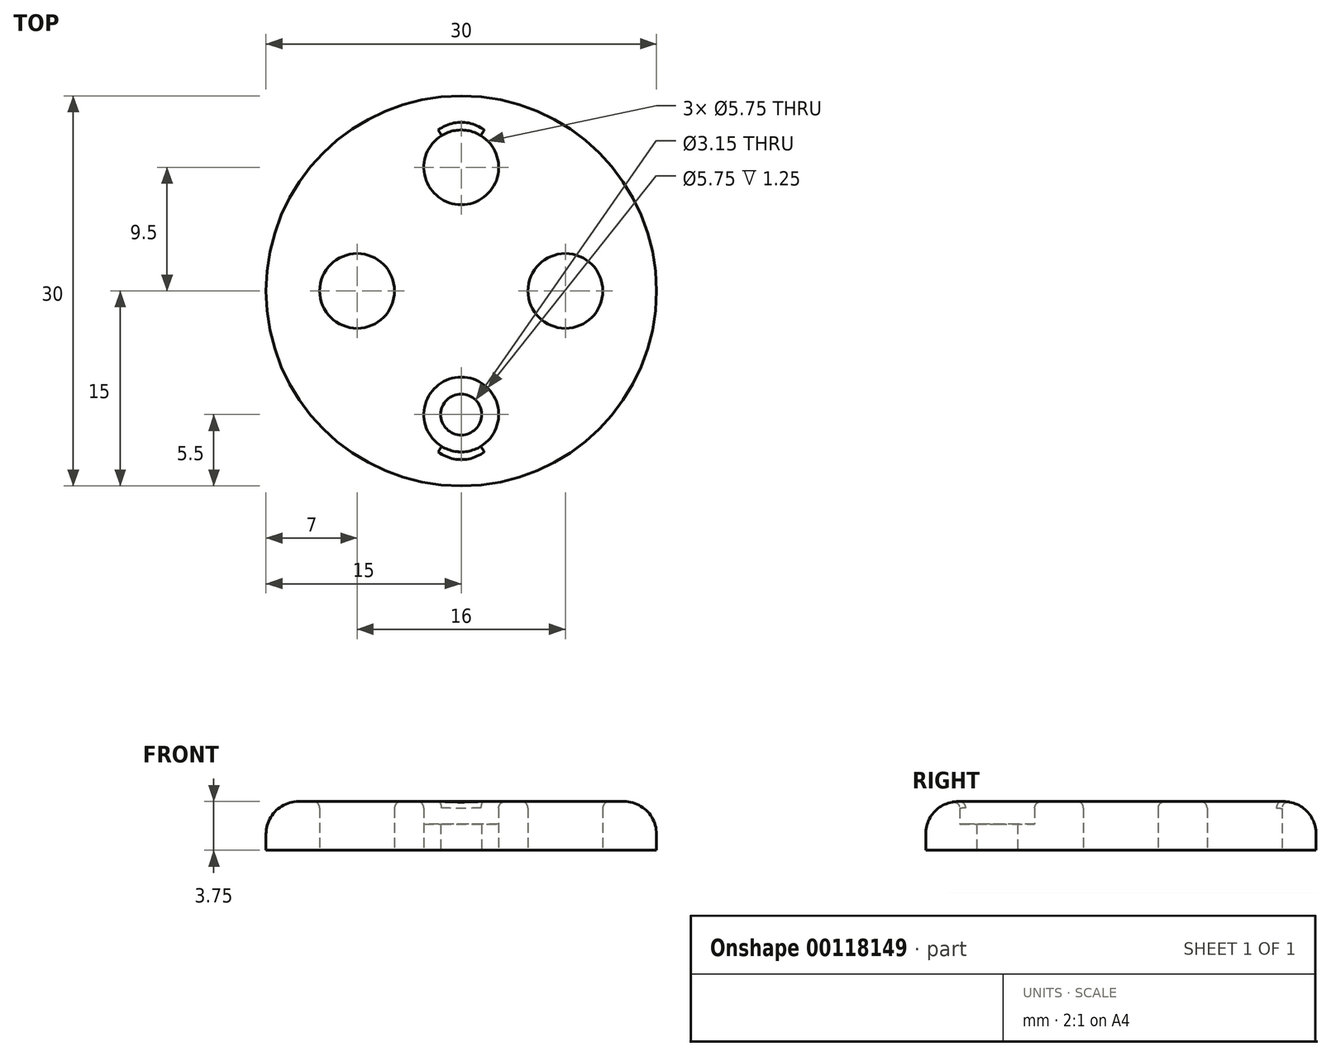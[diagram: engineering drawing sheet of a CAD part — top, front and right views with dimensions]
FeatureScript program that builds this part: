
annotation { "Feature Type Name" : "Feature", "Feature Type Description" : "" }
export const myFeature = defineFeature(function(context is Context, id is Id, definition is map)
    precondition{}
    {
        {
            var Q0;
            Q0=qCreatedBy(makeId("Top.planeOp"),FACE);
            var sketch = newSketch(context, id + "F0", { "sketchPlane" : qUnion([Q0])});
            skCircle(sketch, "E0", {"center": v(0, 0) * mm, "radius": 15 * mm});
            skLineSegment(sketch, "E1", {"start": v(0, 15) * mm, "end": v(0, -15) * mm});
            skLineSegment(sketch, "E2", {"start": v(-19.9, 0) * mm, "end": v(23, 0) * mm});
            skCircle(sketch, "E3", {"center": v(-8, 0) * mm, "radius": 1.57 * mm});
            skCircle(sketch, "E4", {"center": v(0, 9.5) * mm, "radius": 1.57 * mm});
            skCircle(sketch, "E5", {"center": v(8, 0) * mm, "radius": 1.57 * mm});
            skCircle(sketch, "E6", {"center": v(0, -9.5) * mm, "radius": 1.57 * mm});
            skCircle(sketch, "E7", {"center": v(-8, 0) * mm, "radius": 2.88 * mm});
            skCircle(sketch, "E8", {"center": v(0, -9.5) * mm, "radius": 2.88 * mm});
            skCircle(sketch, "E9", {"center": v(8, 0) * mm, "radius": 2.88 * mm});
            skCircle(sketch, "E10", {"center": v(0, 9.5) * mm, "radius": 2.88 * mm});
            skSolve(sketch);
        }
        {
            var Q0;
            Q0=qSketchRegion(id+"F0",true);
            var Q1;
            {var subQ1=sQuery(id+"F0.wireOp",EDGE,"E0");var subQ6=sQuery(id+"F0.wireOp",EDGE,"E1");var subQ9=makeQuery(id+"F0.imprint","INTERSECT",VERTEX,{"disambiguationData":[OD(0.0)],"derivedFrom":[subQ1,subQ6]});Q1=makeQuery(id+"F0.imprint","IMPRINT",FACE,{"disambiguationData":[TD([[makeQuery(id+"F0.imprint","IMPRINT",EDGE,{"disambiguationData":[TD([[subQ9,-1.0]])],"derivedFrom":subQ1}),1.0]])]});}
            var Q2;
            {var subQ0=sQuery(id+"F0.wireOp",EDGE,"E2");var subQ1=sQuery(id+"F0.wireOp",EDGE,"E0");var subQ2=makeQuery(id+"F0.imprint","INTERSECT",VERTEX,{"disambiguationData":[OD(1.0)],"derivedFrom":[subQ1,subQ0]});Q2=makeQuery(id+"F0.imprint","IMPRINT",FACE,{"disambiguationData":[TD([[makeQuery(id+"F0.imprint","IMPRINT",EDGE,{"disambiguationData":[TD([[subQ2,-1.0]])],"derivedFrom":subQ1}),1.0]])]});}
            var Q3;
            {var subQ0=sQuery(id+"F0.wireOp",EDGE,"E7");var subQ1=sQuery(id+"F0.wireOp",EDGE,"E2");var subQ2=makeQuery(id+"F0.imprint","INTERSECT",VERTEX,{"disambiguationData":[OD(0.0)],"derivedFrom":[subQ1,subQ0]});Q3=makeQuery(id+"F0.imprint","IMPRINT",FACE,{"disambiguationData":[TD([[makeQuery(id+"F0.imprint","IMPRINT",EDGE,{"disambiguationData":[TD([[subQ2,-1.0]])],"derivedFrom":subQ1}),1.0]])]});}
            var Q4;
            {var subQ0=sQuery(id+"F0.wireOp",EDGE,"E7");var subQ1=sQuery(id+"F0.wireOp",EDGE,"E2");var subQ2=makeQuery(id+"F0.imprint","INTERSECT",VERTEX,{"disambiguationData":[OD(0.0)],"derivedFrom":[subQ1,subQ0]});Q4=makeQuery(id+"F0.imprint","IMPRINT",FACE,{"disambiguationData":[TD([[makeQuery(id+"F0.imprint","IMPRINT",EDGE,{"disambiguationData":[TD([[subQ2,-1.0]])],"derivedFrom":subQ1}),-1.0]])]});}
            var Q5;
            {var subQ0=sQuery(id+"F0.wireOp",EDGE,"E8");var subQ1=sQuery(id+"F0.wireOp",EDGE,"E1");var subQ2=makeQuery(id+"F0.imprint","INTERSECT",VERTEX,{"disambiguationData":[OD(0.0)],"derivedFrom":[subQ1,subQ0]});Q5=makeQuery(id+"F0.imprint","IMPRINT",FACE,{"disambiguationData":[TD([[makeQuery(id+"F0.imprint","IMPRINT",EDGE,{"disambiguationData":[TD([[subQ2,-1.0]])],"derivedFrom":subQ1}),-1.0]])]});}
            var Q6;
            {var subQ0=sQuery(id+"F0.wireOp",EDGE,"E8");var subQ1=sQuery(id+"F0.wireOp",EDGE,"E1");var subQ2=makeQuery(id+"F0.imprint","INTERSECT",VERTEX,{"disambiguationData":[OD(0.0)],"derivedFrom":[subQ1,subQ0]});Q6=makeQuery(id+"F0.imprint","IMPRINT",FACE,{"disambiguationData":[TD([[makeQuery(id+"F0.imprint","IMPRINT",EDGE,{"disambiguationData":[TD([[subQ2,-1.0]])],"derivedFrom":subQ1}),1.0]])]});}
            var Q7;
            {var subQ0=sQuery(id+"F0.wireOp",EDGE,"E9");var subQ1=sQuery(id+"F0.wireOp",EDGE,"E2");var subQ2=makeQuery(id+"F0.imprint","INTERSECT",VERTEX,{"disambiguationData":[OD(0.0)],"derivedFrom":[subQ1,subQ0]});Q7=makeQuery(id+"F0.imprint","IMPRINT",FACE,{"disambiguationData":[TD([[makeQuery(id+"F0.imprint","IMPRINT",EDGE,{"disambiguationData":[TD([[subQ2,-1.0]])],"derivedFrom":subQ1}),-1.0]])]});}
            var Q8;
            {var subQ0=sQuery(id+"F0.wireOp",EDGE,"E9");var subQ1=sQuery(id+"F0.wireOp",EDGE,"E2");var subQ2=makeQuery(id+"F0.imprint","INTERSECT",VERTEX,{"disambiguationData":[OD(0.0)],"derivedFrom":[subQ1,subQ0]});Q8=makeQuery(id+"F0.imprint","IMPRINT",FACE,{"disambiguationData":[TD([[makeQuery(id+"F0.imprint","IMPRINT",EDGE,{"disambiguationData":[TD([[subQ2,-1.0]])],"derivedFrom":subQ1}),1.0]])]});}
            var Q9;
            {var subQ0=sQuery(id+"F0.wireOp",EDGE,"E10");var subQ1=sQuery(id+"F0.wireOp",EDGE,"E1");var subQ2=makeQuery(id+"F0.imprint","INTERSECT",VERTEX,{"disambiguationData":[OD(0.0)],"derivedFrom":[subQ1,subQ0]});Q9=makeQuery(id+"F0.imprint","IMPRINT",FACE,{"disambiguationData":[TD([[makeQuery(id+"F0.imprint","IMPRINT",EDGE,{"disambiguationData":[TD([[subQ2,-1.0]])],"derivedFrom":subQ1}),1.0]])]});}
            var Q10;
            {var subQ0=sQuery(id+"F0.wireOp",EDGE,"E10");var subQ1=sQuery(id+"F0.wireOp",EDGE,"E1");var subQ2=makeQuery(id+"F0.imprint","INTERSECT",VERTEX,{"disambiguationData":[OD(0.0)],"derivedFrom":[subQ1,subQ0]});Q10=makeQuery(id+"F0.imprint","IMPRINT",FACE,{"disambiguationData":[TD([[makeQuery(id+"F0.imprint","IMPRINT",EDGE,{"disambiguationData":[TD([[subQ2,-1.0]])],"derivedFrom":subQ1}),-1.0]])]});}
            extrude(context, id + "F1", {"entities" : qUnion([Q0, Q1, Q2, Q3, Q4, Q5, Q6, Q7, Q8, Q9, Q10]), "depth" : 2 * mm});
        }
        {
            var Q0;
            {var subQ1=sQuery(id+"F0.wireOp",EDGE,"E0");var subQ5=sQuery(id+"F0.wireOp",EDGE,"E1");var subQ10=makeQuery(id+"F0.imprint","INTERSECT",VERTEX,{"disambiguationData":[OD(0.0)],"derivedFrom":[subQ1,subQ5]});Q0=makeQuery(id+"F0.imprint","IMPRINT",FACE,{"disambiguationData":[TD([[makeQuery(id+"F0.imprint","IMPRINT",EDGE,{"disambiguationData":[TD([[subQ10,-1.0]])],"derivedFrom":subQ1}),1.0]])]});}
            var Q1;
            {var subQ1=sQuery(id+"F0.wireOp",EDGE,"E0");var subQ5=sQuery(id+"F0.wireOp",EDGE,"E1");var subQ8=makeQuery(id+"F0.imprint","INTERSECT",VERTEX,{"disambiguationData":[OD(1.0)],"derivedFrom":[subQ1,subQ5]});Q1=makeQuery(id+"F0.imprint","IMPRINT",FACE,{"disambiguationData":[TD([[makeQuery(id+"F0.imprint","IMPRINT",EDGE,{"disambiguationData":[TD([[subQ8,1.0]])],"derivedFrom":subQ1}),1.0]])]});}
            var Q2;
            {var subQ1=sQuery(id+"F0.wireOp",EDGE,"E1");var subQ5=sQuery(id+"F0.wireOp",EDGE,"E0");var subQ6=makeQuery(id+"F0.imprint","INTERSECT",VERTEX,{"disambiguationData":[OD(1.0)],"derivedFrom":[subQ5,subQ1]});Q2=makeQuery(id+"F0.imprint","IMPRINT",FACE,{"disambiguationData":[TD([[makeQuery(id+"F0.imprint","IMPRINT",EDGE,{"disambiguationData":[TD([[subQ6,-1.0]])],"derivedFrom":subQ5}),1.0]])]});}
            var Q3;
            {var subQ1=sQuery(id+"F0.wireOp",EDGE,"E1");var subQ7=sQuery(id+"F0.wireOp",EDGE,"E0");var subQ8=makeQuery(id+"F0.imprint","INTERSECT",VERTEX,{"disambiguationData":[OD(0.0)],"derivedFrom":[subQ7,subQ1]});Q3=makeQuery(id+"F0.imprint","IMPRINT",FACE,{"disambiguationData":[TD([[makeQuery(id+"F0.imprint","IMPRINT",EDGE,{"disambiguationData":[TD([[subQ8,1.0]])],"derivedFrom":subQ7}),1.0]])]});}
            extrude(context, id + "F2", {"entities" : qUnion([Q0, Q1, Q2, Q3]), "operationType" : NewBodyOperationType.ADD, "depth" : 3.75 * mm});
        }
        {
            var Q0;
            Q0=makeQuery(id+"F2.opExtrude","CAP_EDGE",EDGE,{"disambiguationData":[OSD([sQuery(id+"F0.wireOp",EDGE,"E0")])],"isStart":false});
            fillet(context, id + "F3", {"entities" : qUnion([Q0]), "radius" : 2.5 * mm, "tangentPropagation" : true, "allowEdgeOverflow" : false});
        }
        {
            var Q0;
            Q0=makeQuery(id+"F2.opExtrude","CAP_EDGE",EDGE,{"disambiguationData":[OSD([sQuery(id+"F0.wireOp",EDGE,"E10")])],"isStart":false});
            var Q1;
            Q1=makeQuery(id+"F2.opExtrude","CAP_EDGE",EDGE,{"disambiguationData":[OSD([sQuery(id+"F0.wireOp",EDGE,"E7")])],"isStart":false});
            var Q2;
            Q2=makeQuery(id+"F2.opExtrude","CAP_EDGE",EDGE,{"disambiguationData":[OSD([sQuery(id+"F0.wireOp",EDGE,"E8")])],"isStart":false});
            var Q3;
            Q3=makeQuery(id+"F2.opExtrude","CAP_EDGE",EDGE,{"disambiguationData":[OSD([sQuery(id+"F0.wireOp",EDGE,"E9")])],"isStart":false});
            fillet(context, id + "F4", {"entities" : qUnion([Q0, Q1, Q2, Q3]), "radius" : .5 * mm, "tangentPropagation" : true, "allowEdgeOverflow" : false});
        }
    });
